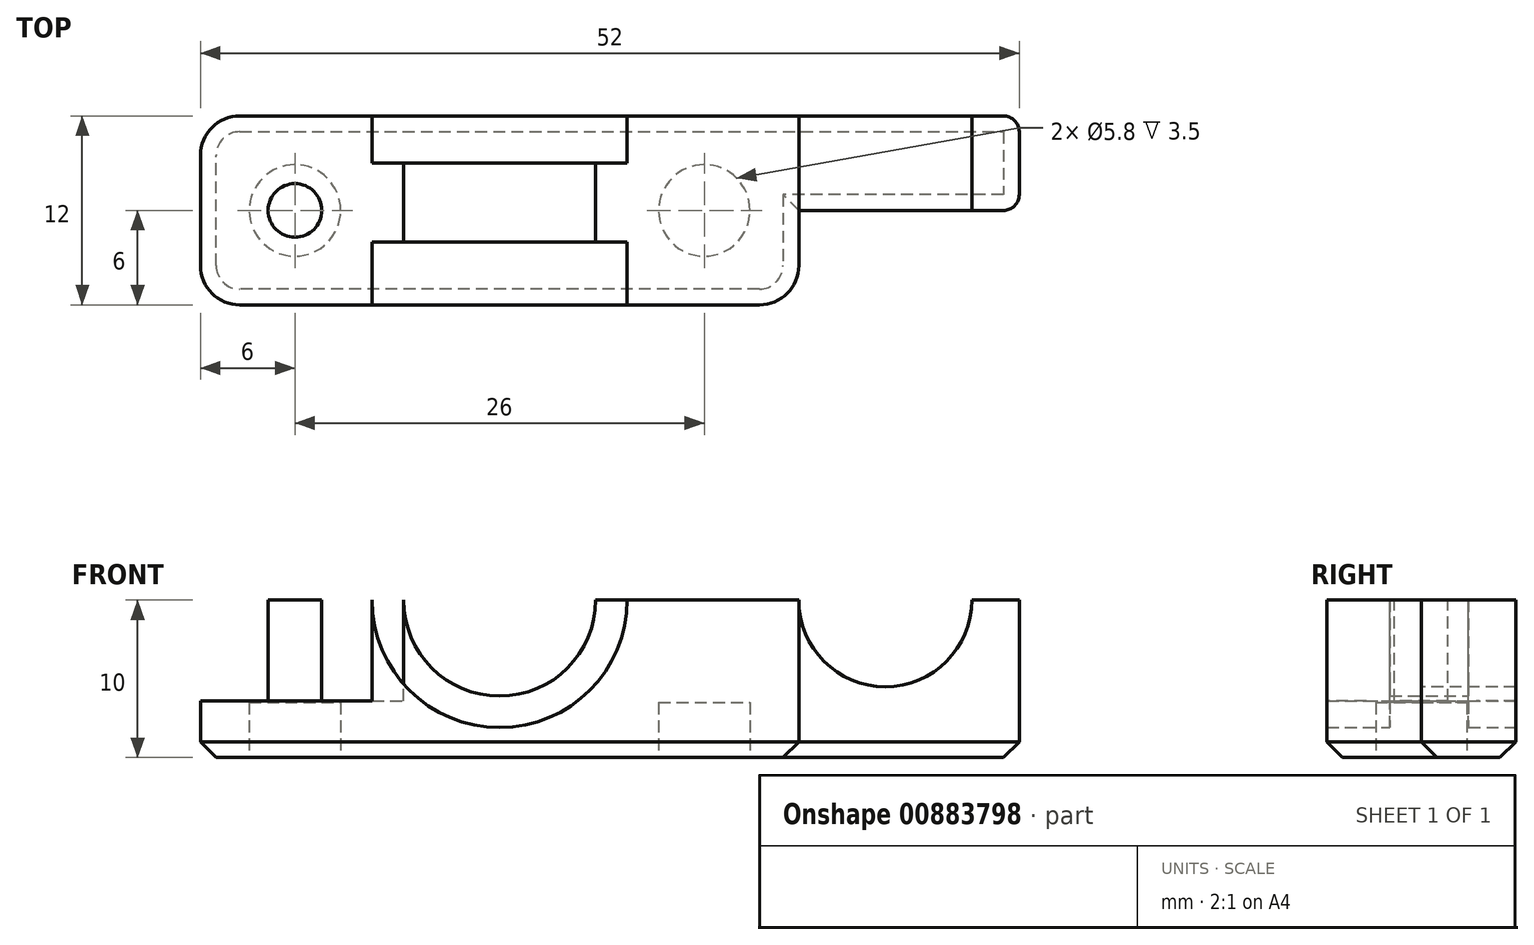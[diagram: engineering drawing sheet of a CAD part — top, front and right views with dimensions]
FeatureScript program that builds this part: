
annotation { "Feature Type Name" : "Feature", "Feature Type Description" : "" }
export const myFeature = defineFeature(function(context is Context, id is Id, definition is map)
    precondition{}
    {
        {
            var Q0;
            Q0=qCreatedBy(makeId("Front.planeOp"),FACE);
            var sketch = newSketch(context, id + "F0", { "sketchPlane" : qUnion([Q0])});
            skLineSegment(sketch, "E0.MirrorCS", {"start": v(19, 10) * mm, "end": v(6.1, 10) * mm});
            skLineSegment(sketch, "E1.MirrorCS", {"start": v(-19, 10) * mm, "end": v(-6.1, 10) * mm});
            skArc(sketch, "E2", {"start": v(-6.1, 10) * mm, "mid": v(0, 3.9) * mm, "end": v(6.1, 10) * mm});
            skArc(sketch, "E3", {"start": v(-8.1, 10) * mm, "mid": v(0, 1.9) * mm, "end": v(8.1, 10) * mm});
            skCircle(sketch, "E4", {"center": v(24.5, 10) * mm, "radius": 5.5 * mm});
            skLineSegment(sketch, "E5", {"start": v(30, 10) * mm, "end": v(33, 10) * mm});
            skLineSegment(sketch, "E6", {"start": v(33, 10) * mm, "end": v(33, 0) * mm});
            skLineSegment(sketch, "E7", {"start": v(33, 0) * mm, "end": v(-19, 0) * mm});
            skLineSegment(sketch, "E8", {"start": v(-19, 0) * mm, "end": v(-19, 10) * mm});
            skLineSegment(sketch, "E9", {"start": v(19, 10) * mm, "end": v(19, 0) * mm});
            skSolve(sketch);
        }
        {
            var Q0;
            {var subQ6=sQuery(id+"F0.wireOp",EDGE,"E3");Q0=makeQuery(id+"F0.imprint","IMPRINT",FACE,{"disambiguationData":[TD([[makeQuery(id+"F0.imprint","IMPRINT",EDGE,{"derivedFrom":subQ6}),-1.0]])]});}
            extrude(context, id + "F1", {"entities" : qUnion([Q0]), "depth" : 12 * mm, "offsetDistance" : 25 * mm, "symmetric" : true});
        }
        {
            var Q0;
            {var subQ0=sQuery(id+"F0.wireOp",EDGE,"E2");Q0=makeQuery(id+"F0.imprint","IMPRINT",FACE,{"disambiguationData":[TD([[makeQuery(id+"F0.imprint","IMPRINT",EDGE,{"derivedFrom":subQ0}),-1.0]])]});}
            extrude(context, id + "F2", {"entities" : qUnion([Q0]), "operationType" : NewBodyOperationType.ADD, "depth" : 2 * mm, "offsetDistance" : 25 * mm, "hasSecondDirection" : true, "secondDirectionOppositeDirection" : true, "secondDirectionDepth" : 3 * mm});
        }
        {
            var Q0;
            {var subQ3=sQuery(id+"F0.wireOp",EDGE,"E5");Q0=makeQuery(id+"F0.imprint","IMPRINT",FACE,{"disambiguationData":[TD([[makeQuery(id+"F0.imprint","IMPRINT",EDGE,{"derivedFrom":subQ3}),-1.0]])]});}
            extrude(context, id + "F3", {"entities" : qUnion([Q0]), "operationType" : NewBodyOperationType.ADD, "oppositeDirection" : true, "depth" : 6 * mm, "offsetDistance" : 25 * mm});
        }
        {
            var Q0;
            Q0=makeQuery(id+"F1.opExtrude","SWEPT_FACE",FACE,{"disambiguationData":[OSD([sQuery(id+"F0.wireOp",EDGE,"E7")])]});
            var sketch = newSketch(context, id + "F4", { "sketchPlane" : qUnion([Q0])});
            skCircle(sketch, "E10", {"center": v(-13, 0) * mm, "radius": 1.7 * mm});
            skCircle(sketch, "E11", {"center": v(13, 0) * mm, "radius": 1.7 * mm});
            skCircle(sketch, "E12.0", {"center": v(13, 0) * mm, "radius": 2.9 * mm});
            skCircle(sketch, "E13.0", {"center": v(-13, 0) * mm, "radius": 2.9 * mm});
            skSolve(sketch);
        }
        {
            var Q0;
            Q0=makeQuery(id+"F4.imprint","IMPRINT",FACE,{"disambiguationData":[TD([[makeQuery(id+"F4.imprint","IMPRINT",EDGE,{"derivedFrom":sQuery(id+"F4.wireOp",EDGE,"E11")}),-1.0]])]});
            var Q1;
            Q1=makeQuery(id+"F4.imprint","IMPRINT",FACE,{"disambiguationData":[TD([[makeQuery(id+"F4.imprint","IMPRINT",EDGE,{"derivedFrom":sQuery(id+"F4.wireOp",EDGE,"E10")}),-1.0]])]});
            var Q2;
            Q2=makeQuery(id+"F4.imprint","IMPRINT",FACE,{"disambiguationData":[TD([[makeQuery(id+"F4.imprint","IMPRINT",EDGE,{"derivedFrom":sQuery(id+"F4.wireOp",EDGE,"E11")}),1.0]])]});
            var Q3;
            Q3=makeQuery(id+"F4.imprint","IMPRINT",FACE,{"disambiguationData":[TD([[makeQuery(id+"F4.imprint","IMPRINT",EDGE,{"derivedFrom":sQuery(id+"F4.wireOp",EDGE,"E10")}),1.0]])]});
            extrude(context, id + "F5", {"entities" : qUnion([Q0, Q1, Q2, Q3]), "operationType" : NewBodyOperationType.REMOVE, "oppositeDirection" : true, "depth" : 3.5 * mm, "offsetDistance" : 25 * mm});
        }
        {
            var Q0;
            Q0=makeQuery(id+"F1.opExtrude","CAP_EDGE",EDGE,{"disambiguationData":[OSD([sQuery(id+"F0.wireOp",EDGE,"E8")])],"isStart":true});
            var Q1;
            Q1=makeQuery(id+"F1.opExtrude","CAP_EDGE",EDGE,{"disambiguationData":[OSD([sQuery(id+"F0.wireOp",EDGE,"E8")])],"isStart":false});
            fillet(context, id + "F6", {"entities" : qUnion([Q0, Q1]), "radius" : 2.5 * mm, "tangentPropagation" : true, "allowEdgeOverflow" : false});
        }
        {
            var Q0;
            Q0=makeQuery(id+"F1.opExtrude","CAP_EDGE",EDGE,{"disambiguationData":[OSD([sQuery(id+"F0.wireOp",EDGE,"E9")])],"isStart":false});
            var Q1;
            Q1=makeQuery(id+"F3.opExtrude","CAP_EDGE",EDGE,{"disambiguationData":[OSD([sQuery(id+"F0.wireOp",EDGE,"E9")])],"isStart":true});
            fillet(context, id + "F7", {"entities" : qUnion([Q0, Q1]), "radius" : 2.5 * mm, "tangentPropagation" : true, "allowEdgeOverflow" : false});
        }
        {
            var Q0;
            Q0=makeQuery(id+"F3.opExtrude","CAP_EDGE",EDGE,{"disambiguationData":[OSD([sQuery(id+"F0.wireOp",EDGE,"E6")])],"isStart":false});
            var Q1;
            Q1=makeQuery(id+"F3.opExtrude","CAP_EDGE",EDGE,{"disambiguationData":[OSD([sQuery(id+"F0.wireOp",EDGE,"E6")])],"isStart":true});
            fillet(context, id + "F8", {"entities" : qUnion([Q0, Q1]), "radius" : 1 * mm, "tangentPropagation" : true, "allowEdgeOverflow" : false});
        }
        {
            var Q0;
            Q0=makeQuery(id+"F5.boolean.opBoolean","COPY",EDGE,{"derivedFrom":makeQuery(id+"F5.opExtrude","CAP_EDGE",EDGE,{"disambiguationData":[OSD([sQuery(id+"F4.wireOp",EDGE,"E13.0")])],"isStart":true})});
            var Q1;
            Q1=makeQuery(id+"F5.boolean.opBoolean","COPY",EDGE,{"derivedFrom":makeQuery(id+"F5.opExtrude","CAP_EDGE",EDGE,{"disambiguationData":[OSD([sQuery(id+"F4.wireOp",EDGE,"E12.0")])],"isStart":true})});
            var Q2;
            Q2=makeQuery(id+"F1.opExtrude","CAP_EDGE",EDGE,{"disambiguationData":[OSD([sQuery(id+"F0.wireOp",EDGE,"E7")])],"isStart":true});
            chamfer(context, id + "F9", {"entities" : qUnion([Q0, Q1, Q2]), "width" : 1 * mm, "tangentPropagation" : true});
        }
        {
            var Q0;
            {var subQ0=sQuery(id+"F0.wireOp",EDGE,"E1.MirrorCS");Q0=makeQuery(id+"F2.boolean.opBoolean","MERGE",FACE,{"derivedFrom":[makeQuery(id+"F1.opExtrude","SWEPT_FACE",FACE,{"disambiguationData":[OSD([subQ0])]}),makeQuery(id+"F2.opExtrude","SWEPT_FACE",FACE,{"disambiguationData":[OSD([subQ0])]})]});}
            var sketch = newSketch(context, id + "F10", { "sketchPlane" : qUnion([Q0])});
            skCircle(sketch, "E14.0", {"center": v(-13, 0) * mm, "radius": 1.7 * mm});
            skCircle(sketch, "E14.1", {"center": v(13, 0) * mm, "radius": 1.7 * mm});
            skSolve(sketch);
        }
        {
            var Q0;
            Q0=makeQuery(id+"F10.imprint","IMPRINT",FACE,{"disambiguationData":[TD([[makeQuery(id+"F10.imprint","IMPRINT",EDGE,{"derivedFrom":sQuery(id+"F10.wireOp",EDGE,"E14.0")}),-1.0]])]});
            var Q1;
            Q1=makeQuery(id+"F10.imprint","IMPRINT",FACE,{"disambiguationData":[TD([[makeQuery(id+"F10.imprint","IMPRINT",EDGE,{"derivedFrom":sQuery(id+"F10.wireOp",EDGE,"E14.1")}),-1.0]])]});
            extrude(context, id + "F11", {"entities" : qUnion([Q0, Q1]), "operationType" : NewBodyOperationType.REMOVE, "oppositeDirection" : true, "depth" : 6.4 * mm, "offsetDistance" : 25 * mm});
        }
    });
